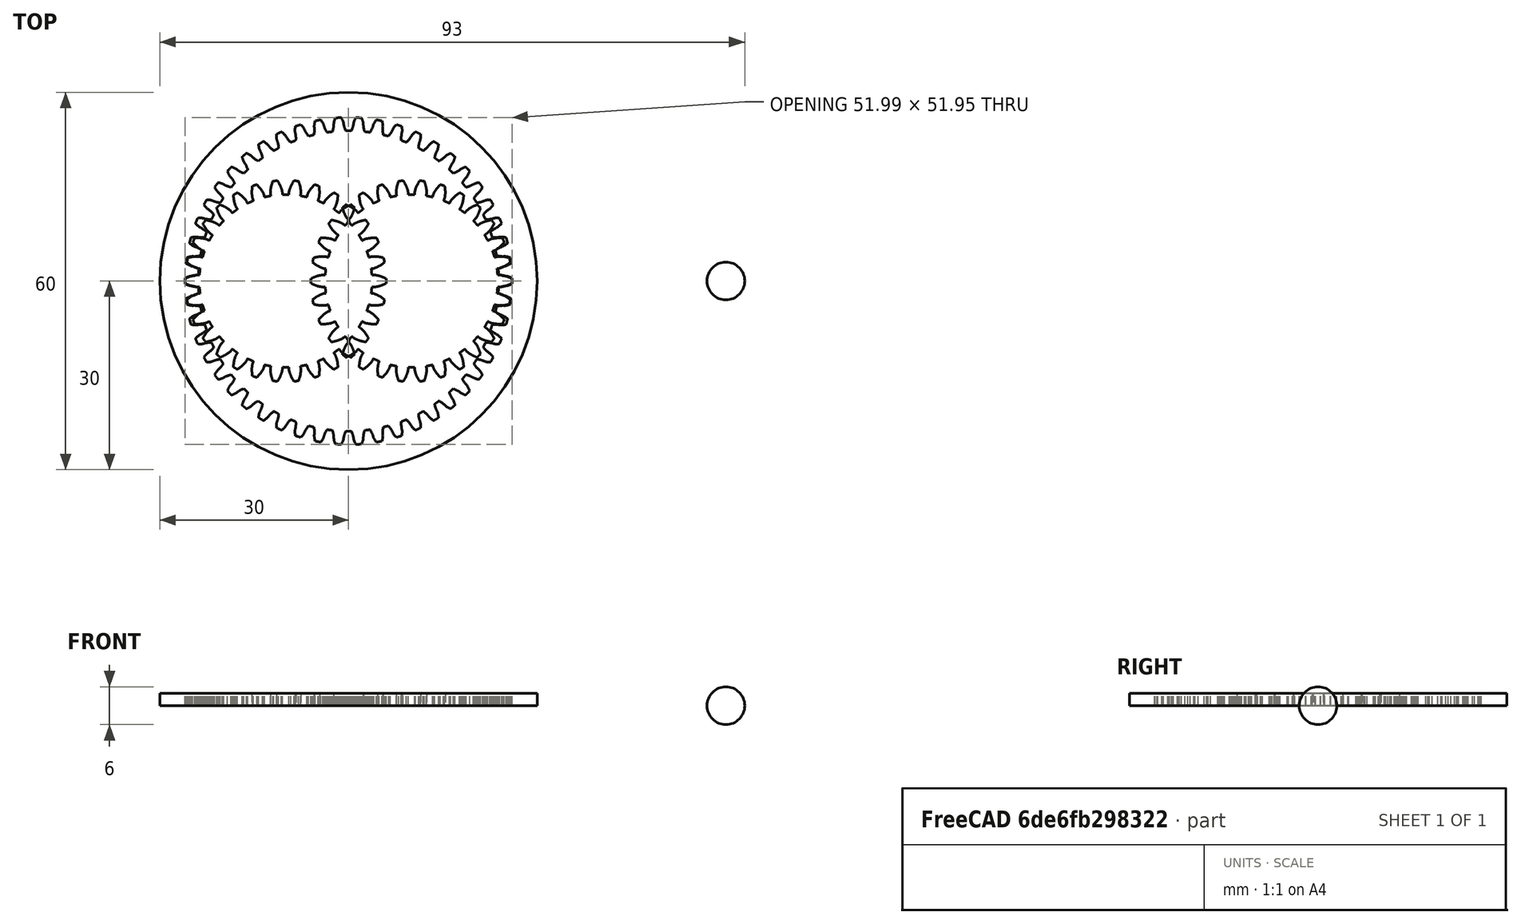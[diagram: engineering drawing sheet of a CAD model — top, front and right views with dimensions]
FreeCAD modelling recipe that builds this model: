
FCSTD DOCUMENT  (FreeCAD 0.18R14555 (Git shallow))
Label: HIPOTROCOIDE
License: All rights reserved
LicenseURL: http://en.wikipedia.org/wiki/All_rights_reserved
objects: Part::Part2DObjectPython×3, Part::FeaturePython×2, Part::Compound×2, App::DocumentObjectGroupPython×2, Part::Cylinder×1, Part::Cut×1, Part::Sphere×1
note: 10 computed .brp shape members not serialized (recipe doc carries the construction recipe); baked Part::Feature solids carry a one-line shape summary decoded from their .brp

FEATURE [Part::FeaturePython] CycloidGear  # WARN: FeaturePython — macro-defined, semantics opaque (R4)
  backlash = 0
  beta = 0
  clearance = 0.25
  double_helix = false
  height = 2
  inner_diameter = 5
  module = 1
  numpoints = 15
  outer_diameter = 5
  teeth = 50
FEATURE [Part::FeaturePython] InvoluteGear  # WARN: FeaturePython — macro-defined, semantics opaque (R4)
  backlash = 0
  beta = 0
  clearance = 0.25
  double_helix = false
  dw = 30
  head = 0
  height = 2
  module = 1
  numpoints = 6
  pressure_angle = 20
  reversed_backlash = false
  shift = 0
  simple = false
  teeth = 30
  undercut = false
FEATURE [Part::Cylinder] Cylinder
  Angle = 360
  AttacherType = Attacher::AttachEngine3D
  Height = 2
  Radius = 30
FEATURE [Part::Cut] Cut
  Base = -> Cylinder
  Tool = -> CycloidGear
FEATURE [Part::Part2DObjectPython] Line  # Draft 2D object (typed FeaturePython)
  ChamferSize = 0
  Closed = false
  End = (50,3.1e-15,0)
  FilletRadius = 0
  Length = 50
  MakeFace = true
  Points = (2) [(0,0,0),(50,1.53081e-15,0)]
  Start = (0,0,0)
  Subdivisions = 0
FEATURE [Part::Compound] Compound
  Links = -> [InvoluteGear,Line]
  Placement = pos=(-10,3.7e-15,0) rot=(0,0,1;0rad)
FEATURE [Part::Part2DObjectPython] BSpline  # Draft 2D object (typed FeaturePython)
  Closed = false
  MakeFace = true
  Parameterization = 1
  Points = (23) [(59.9681,3.05966e-15,0),(58.6435,-6.56508,0),(51.0379,-17.2053,0),(37.6147,-27.0396,0),(20.0356,-35.3202,0),(0.645829,-41.3349,0),+17 more]
FEATURE [Part::Part2DObjectPython] Clone2D  label="BSpline (2D)"  # Draft 2D object (typed FeaturePython)
  Fuse = false
  Objects = -> [BSpline]
  Placement = pos=(0,0,0) rot=(1,0,0;3.14159rad)
  Scale = (1,1,1)
FEATURE [Part::Sphere] Sphere
  Angle1 = -90
  Angle2 = 90
  Angle3 = 360
  AttacherType = Attacher::AttachEngine3D
  Placement = pos=(50,0,0) rot=(0,0,1;0rad)
  Radius = 3
FEATURE [Part::Compound] Compound001
  Links = -> [InvoluteGear,Line,Sphere]
  Placement = pos=(10,3.43e-14,0) rot=(0,0,1;0rad)
FEATURE [App::DocumentObjectGroupPython] My_Placer  # scripted group (container) (typed FeaturePython)
  Placement = pos=(10,3.43e-14,0) rot=(0,0,1;-62.8319rad)
  RotAxis = (0,0,1)
  RotCenter = (0,0,0)
  arc = -time*360
  arc0 = 0
  arc1 = 90
  target = -> Compound001
  time = 10
  x = x0*10
  x0 = 1
  x1 = 200
  y = y0*10
  y0 = 3.4e-15
  y1 = 0
  z = 0
  z0 = 0
  z1 = 0
  expr: y0 = sin(time * 540)
  expr: x0 = cos(time * 540)
FEATURE [App::DocumentObjectGroupPython] My_Manager  # scripted group (container) (typed FeaturePython)
  Group = -> [My_Placer]
  intervall = 1000
  sleeptime = 0.02
  start = 0
  step = 1000
  text = NO
